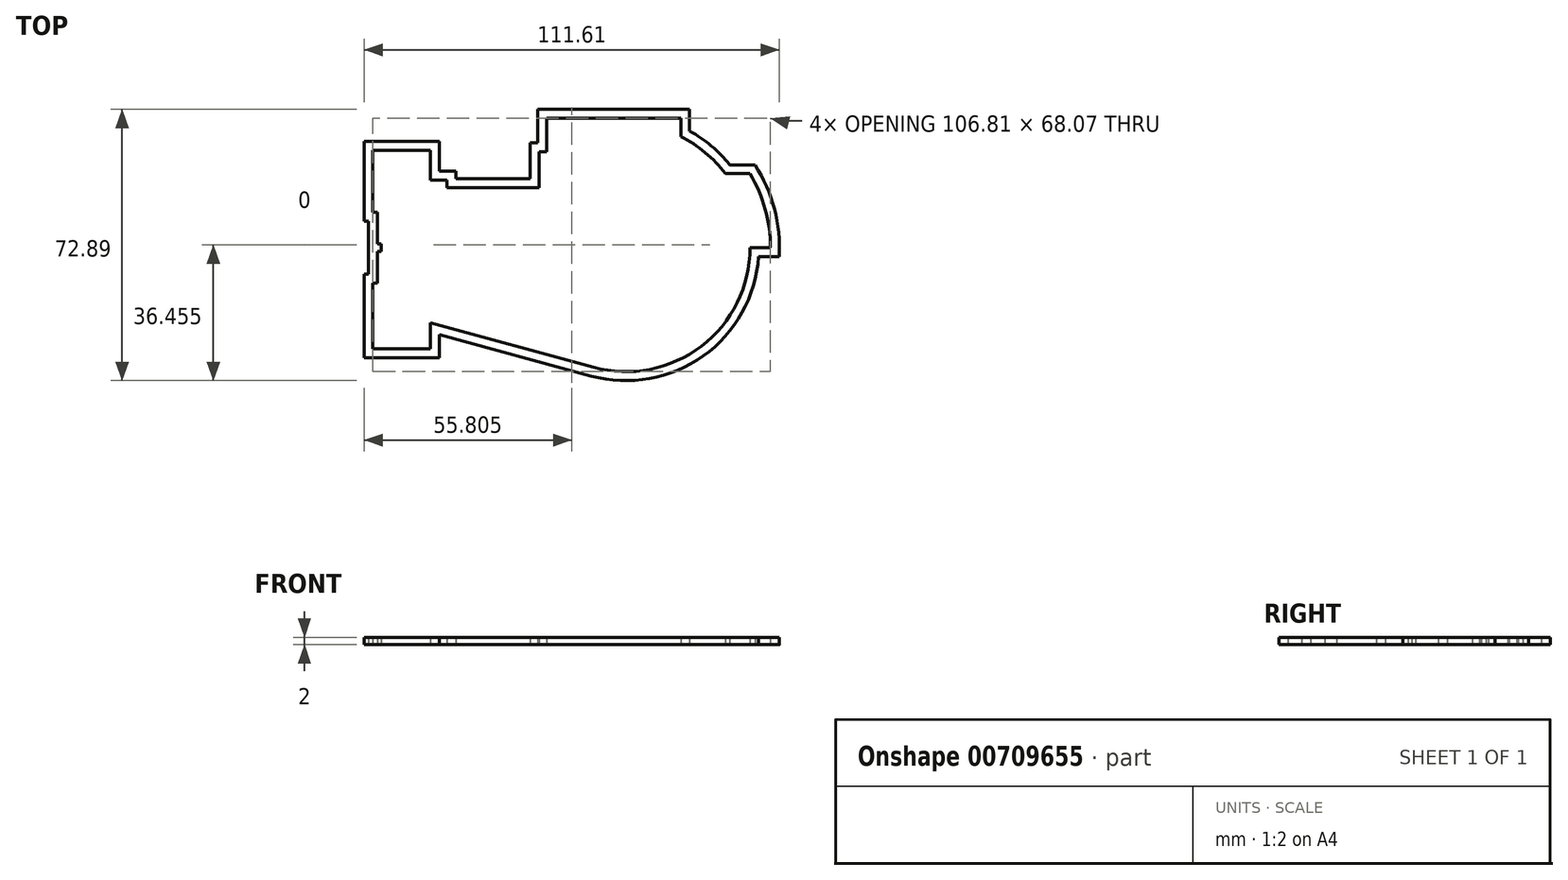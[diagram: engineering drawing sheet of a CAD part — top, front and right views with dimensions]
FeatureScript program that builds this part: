
annotation { "Feature Type Name" : "Feature", "Feature Type Description" : "" }
export const myFeature = defineFeature(function(context is Context, id is Id, definition is map)
    precondition{}
    {
        {
            var Q0;
            Q0=qCreatedBy(makeId("Top.planeOp"),FACE);
            var sketch = newSketch(context, id + "F0", { "sketchPlane" : qUnion([Q0])});
            skArc(sketch, "E0", {"start": v(-8.74, -32.13) * mm, "mid": v(20.22, -26.46) * mm, "end": v(33.3, 0) * mm});
            skArc(sketch, "E1", {"start": v(38.8, 0) * mm, "mid": v(37.4, 10.33) * mm, "end": v(33.3, 19.91) * mm});
            skLineSegment(sketch, "E2", {"start": v(33.3, 0) * mm, "end": v(38.8, 0) * mm});
            skLineSegment(sketch, "E3", {"start": v(33.3, 19.91) * mm, "end": v(26.69, 19.91) * mm});
            skLineSegment(sketch, "E4", {"start": v(-21.31, 25.79) * mm, "end": v(-23.31, 25.79) * mm});
            skArc(sketch, "E5.trimOffspring", {"start": v(26.69, 19.91) * mm, "mid": v(21.28, 25.61) * mm, "end": v(14.69, 29.88) * mm});
            skLineSegment(sketch, "E6.MirrorCS", {"start": v(-68.01, -9.5) * mm, "end": v(-66.81, -9.5) * mm});
            skLineSegment(sketch, "E7.MirrorCS", {"start": v(-65.81, -1) * mm, "end": v(-65.81, 0) * mm});
            skLineSegment(sketch, "E8.MirrorCS", {"start": v(-66.81, -1) * mm, "end": v(-65.81, -1) * mm});
            skLineSegment(sketch, "E9.MirrorCS", {"start": v(-66.81, -9.5) * mm, "end": v(-66.81, -1) * mm});
            skLineSegment(sketch, "E10", {"start": v(-52.61, 26.2) * mm, "end": v(-52.61, 18.2) * mm});
            skLineSegment(sketch, "E11", {"start": v(-23.31, 25.79) * mm, "end": v(-23.31, 16.2) * mm});
            skArc(sketch, "E12", {"start": v(204.58, -8.62) * mm, "mid": v(241.3, -32.1) * mm, "end": v(269.8, 0.86) * mm});
            skArc(sketch, "E13", {"start": v(275.3, 0.86) * mm, "mid": v(273.9, 11.2) * mm, "end": v(269.8, 20.77) * mm});
            skLineSegment(sketch, "E14", {"start": v(269.8, 0.86) * mm, "end": v(275.3, 0.86) * mm});
            skLineSegment(sketch, "E15", {"start": v(269.8, 20.77) * mm, "end": v(263.2, 20.77) * mm});
            skLineSegment(sketch, "E16", {"start": v(263.2, 20.77) * mm, "end": v(248.4, 20.77) * mm, "construction": true});
            skLineSegment(sketch, "E17", {"start": v(248.4, 20.77) * mm, "end": v(248.4, 31.97) * mm, "construction": true});
            skLineSegment(sketch, "E18", {"start": v(248.4, 31.97) * mm, "end": v(248.4, 35.97) * mm});
            skLineSegment(sketch, "E19", {"start": v(248.4, 35.97) * mm, "end": v(218.9, 35.97) * mm});
            skLineSegment(sketch, "E20", {"start": v(218.9, 35.97) * mm, "end": v(218.9, 31.97) * mm});
            skLineSegment(sketch, "E21", {"start": v(218.9, 31.97) * mm, "end": v(214.9, 31.97) * mm});
            skLineSegment(sketch, "E22", {"start": v(214.9, 31.97) * mm, "end": v(214.9, 26.97) * mm});
            skLineSegment(sketch, "E23", {"start": v(214.9, 26.97) * mm, "end": v(212.9, 26.97) * mm});
            skLineSegment(sketch, "E24", {"start": v(183.9, 26.06) * mm, "end": v(169.9, 26.06) * mm});
            skLineSegment(sketch, "E25", {"start": v(169.9, 26.06) * mm, "end": v(169.9, 10.36) * mm});
            skLineSegment(sketch, "E26", {"start": v(169.9, 10.36) * mm, "end": v(171.1, 10.36) * mm});
            skLineSegment(sketch, "E27", {"start": v(171.1, 10.36) * mm, "end": v(171.1, 1.86) * mm});
            skLineSegment(sketch, "E28", {"start": v(171.1, 1.86) * mm, "end": v(172.1, 1.86) * mm});
            skArc(sketch, "E29.trimOffspring", {"start": v(263.2, 20.77) * mm, "mid": v(256.6, 27.42) * mm, "end": v(248.4, 31.97) * mm});
            skLineSegment(sketch, "E30", {"start": v(172.1, 1.86) * mm, "end": v(172.1, 0.86) * mm});
            skLineSegment(sketch, "E31.MirrorCS", {"start": v(169.9, -8.64) * mm, "end": v(171.1, -8.64) * mm});
            skLineSegment(sketch, "E32.MirrorCS", {"start": v(172.1, -0.14) * mm, "end": v(172.1, 0.86) * mm});
            skLineSegment(sketch, "E33.MirrorCS", {"start": v(171.1, -0.14) * mm, "end": v(172.1, -0.14) * mm});
            skLineSegment(sketch, "E34.MirrorCS", {"start": v(183.9, -24.34) * mm, "end": v(169.9, -24.34) * mm});
            skLineSegment(sketch, "E35.MirrorCS", {"start": v(171.1, -8.64) * mm, "end": v(171.1, -0.14) * mm});
            skLineSegment(sketch, "E36.MirrorCS", {"start": v(169.9, -24.34) * mm, "end": v(169.9, -8.64) * mm});
            skLineSegment(sketch, "E37", {"start": v(183.9, -24.34) * mm, "end": v(183.9, -17.54) * mm});
            skLineSegment(sketch, "E38", {"start": v(183.9, 26.06) * mm, "end": v(183.9, 18.06) * mm});
            skLineSegment(sketch, "E39", {"start": v(183.9, 18.06) * mm, "end": v(186.9, 18.06) * mm});
            skLineSegment(sketch, "E40", {"start": v(186.9, 18.06) * mm, "end": v(186.9, 16.06) * mm});
            skLineSegment(sketch, "E41", {"start": v(186.9, 16.06) * mm, "end": v(213.9, 16.06) * mm});
            skLineSegment(sketch, "E42", {"start": v(212.9, 26.97) * mm, "end": v(212.9, 16.06) * mm});
            skLineSegment(sketch, "E43", {"start": v(183.9, -17.54) * mm, "end": v(226.54, -30.91) * mm});
            skLineSegment(sketch, "E44", {"start": v(-65.81, 0) * mm, "end": v(-65.81, 1) * mm});
            skLineSegment(sketch, "E45", {"start": v(-65.81, 1) * mm, "end": v(-66.81, 1) * mm});
            skLineSegment(sketch, "E46", {"start": v(-66.81, 1) * mm, "end": v(-66.81, 9.5) * mm});
            skLineSegment(sketch, "E47", {"start": v(-66.81, 9.5) * mm, "end": v(-68.01, 9.5) * mm});
            skLineSegment(sketch, "E48", {"start": v(-68.01, 9.5) * mm, "end": v(-68.01, 26.2) * mm});
            skLineSegment(sketch, "E49", {"start": v(-48.11, 16.2) * mm, "end": v(-23.31, 16.2) * mm});
            skLineSegment(sketch, "E50", {"start": v(-68.01, -9.5) * mm, "end": v(-68.01, -27.2) * mm});
            skArc(sketch, "E51", {"start": v(230.7, -116.63) * mm, "mid": v(260.39, -111.7) * mm, "end": v(273.97, -84.85) * mm});
            skArc(sketch, "E52", {"start": v(279.47, -84.85) * mm, "mid": v(278.07, -74.53) * mm, "end": v(273.97, -64.94) * mm});
            skLineSegment(sketch, "E53", {"start": v(273.97, -84.85) * mm, "end": v(279.47, -84.85) * mm});
            skLineSegment(sketch, "E54", {"start": v(273.97, -64.94) * mm, "end": v(267.36, -64.94) * mm});
            skLineSegment(sketch, "E55", {"start": v(253.36, -54.07) * mm, "end": v(253.36, -50.07) * mm});
            skLineSegment(sketch, "E56", {"start": v(253.36, -50.07) * mm, "end": v(223.36, -50.07) * mm});
            skLineSegment(sketch, "E57", {"start": v(223.36, -50.07) * mm, "end": v(223.36, -54.07) * mm});
            skLineSegment(sketch, "E58", {"start": v(223.36, -54.07) * mm, "end": v(219.36, -54.07) * mm});
            skLineSegment(sketch, "E59", {"start": v(219.36, -54.07) * mm, "end": v(219.36, -59.07) * mm});
            skLineSegment(sketch, "E60", {"start": v(219.36, -59.07) * mm, "end": v(217.36, -59.07) * mm});
            skLineSegment(sketch, "E61", {"start": v(188.06, -58.65) * mm, "end": v(174.06, -58.65) * mm});
            skArc(sketch, "E62.trimOffspring", {"start": v(267.36, -64.94) * mm, "mid": v(261.1, -58.56) * mm, "end": v(253.36, -54.07) * mm});
            skLineSegment(sketch, "E63.MirrorCS", {"start": v(174.06, -94.35) * mm, "end": v(175.26, -94.35) * mm});
            skLineSegment(sketch, "E64.MirrorCS", {"start": v(176.26, -85.85) * mm, "end": v(176.26, -84.85) * mm});
            skLineSegment(sketch, "E65.MirrorCS", {"start": v(175.26, -85.85) * mm, "end": v(176.26, -85.85) * mm});
            skLineSegment(sketch, "E66.MirrorCS", {"start": v(175.26, -94.35) * mm, "end": v(175.26, -85.85) * mm});
            skLineSegment(sketch, "E67", {"start": v(188.06, -58.65) * mm, "end": v(188.06, -66.65) * mm});
            skLineSegment(sketch, "E68", {"start": v(188.06, -66.65) * mm, "end": v(191.06, -66.65) * mm});
            skLineSegment(sketch, "E69", {"start": v(191.06, -66.65) * mm, "end": v(191.06, -68.65) * mm});
            skLineSegment(sketch, "E70", {"start": v(217.36, -59.07) * mm, "end": v(217.36, -68.65) * mm});
            skLineSegment(sketch, "E71", {"start": v(240.67, -84.85) * mm, "end": v(176.26, -84.85) * mm});
            skLineSegment(sketch, "E72", {"start": v(176.26, -84.85) * mm, "end": v(176.26, -83.85) * mm});
            skLineSegment(sketch, "E73", {"start": v(176.26, -83.85) * mm, "end": v(175.26, -83.85) * mm});
            skLineSegment(sketch, "E74", {"start": v(175.26, -83.85) * mm, "end": v(175.26, -75.35) * mm});
            skLineSegment(sketch, "E75", {"start": v(175.26, -75.35) * mm, "end": v(174.06, -75.35) * mm});
            skLineSegment(sketch, "E76", {"start": v(174.06, -75.35) * mm, "end": v(174.06, -58.65) * mm});
            skLineSegment(sketch, "E77", {"start": v(191.06, -68.65) * mm, "end": v(217.36, -68.65) * mm});
            skLineSegment(sketch, "E78", {"start": v(174.06, -94.35) * mm, "end": v(174.06, -112.05) * mm});
            skLineSegment(sketch, "E79", {"start": v(174.06, -112.05) * mm, "end": v(188.06, -112.05) * mm});
            skLineSegment(sketch, "E80", {"start": v(188.06, -112.05) * mm, "end": v(188.06, -103.25) * mm});
            skLineSegment(sketch, "E81", {"start": v(188.06, -103.25) * mm, "end": v(230.7, -116.63) * mm});
            skLineSegment(sketch, "E82", {"start": v(-68.01, 26.2) * mm, "end": v(-52.61, 26.2) * mm});
            skLineSegment(sketch, "E83", {"start": v(-68.01, -27.2) * mm, "end": v(-52.61, -27.2) * mm});
            skLineSegment(sketch, "E84", {"start": v(14.69, 34.79) * mm, "end": v(14.69, 29.88) * mm});
            skPoint(sketch, "E85.orphan", {"position": v(12.69, 30.79) * mm});
            skLineSegment(sketch, "E86", {"start": v(-48.11, 18.2) * mm, "end": v(-48.11, 16.2) * mm});
            skPoint(sketch, "E87.orphan", {"position": v(-49.61, 16.2) * mm});
            skLineSegment(sketch, "E88", {"start": v(-52.61, 18.2) * mm, "end": v(-48.11, 18.2) * mm});
            skLineSegment(sketch, "E89", {"start": v(-52.61, -27.2) * mm, "end": v(-52.61, -20.2) * mm});
            skLineSegment(sketch, "E90", {"start": v(-52.61, -20.2) * mm, "end": v(-8.74, -32.13) * mm});
            skLineSegment(sketch, "E91", {"start": v(-21.31, 34.79) * mm, "end": v(14.69, 34.79) * mm});
            skLineSegment(sketch, "E92", {"start": v(-21.31, 34.79) * mm, "end": v(-21.31, 25.79) * mm});
            skLineSegment(sketch, "E93.0", {"start": v(-70.41, -29.6) * mm, "end": v(-50.21, -29.6) * mm});
            skLineSegment(sketch, "E93.1", {"start": v(-23.71, 28.19) * mm, "end": v(-25.71, 28.19) * mm});
            skLineSegment(sketch, "E93.2", {"start": v(-23.71, 37.19) * mm, "end": v(-23.71, 28.19) * mm});
            skLineSegment(sketch, "E93.3", {"start": v(-23.71, 37.19) * mm, "end": v(17.09, 37.19) * mm});
            skLineSegment(sketch, "E93.4", {"start": v(17.09, 37.19) * mm, "end": v(17.09, 31.34) * mm});
            skArc(sketch, "E93.5", {"start": v(27.87, 22.31) * mm, "mid": v(22.93, 27.36) * mm, "end": v(17.09, 31.34) * mm});
            skLineSegment(sketch, "E93.6", {"start": v(34.63, 22.31) * mm, "end": v(27.87, 22.31) * mm});
            skLineSegment(sketch, "E93.7", {"start": v(-50.21, -23.34) * mm, "end": v(-9.37, -34.45) * mm});
            skArc(sketch, "E93.8", {"start": v(-9.37, -34.45) * mm, "mid": v(20.71, -29.08) * mm, "end": v(35.62, -2.4) * mm});
            skLineSegment(sketch, "E93.9", {"start": v(35.62, -2.4) * mm, "end": v(41.13, -2.4) * mm});
            skArc(sketch, "E93.10", {"start": v(41.13, -2.4) * mm, "mid": v(39.85, 10.47) * mm, "end": v(34.63, 22.31) * mm});
            skLineSegment(sketch, "E93.11", {"start": v(-25.71, 28.19) * mm, "end": v(-25.71, 18.6) * mm});
            skLineSegment(sketch, "E93.12", {"start": v(-50.21, -29.6) * mm, "end": v(-50.21, -23.34) * mm});
            skLineSegment(sketch, "E93.13", {"start": v(-45.71, 18.6) * mm, "end": v(-25.71, 18.6) * mm});
            skLineSegment(sketch, "E93.14", {"start": v(-45.71, 20.6) * mm, "end": v(-45.71, 18.6) * mm});
            skLineSegment(sketch, "E93.15", {"start": v(-50.21, 20.6) * mm, "end": v(-45.71, 20.6) * mm});
            skLineSegment(sketch, "E93.16", {"start": v(-50.21, 28.6) * mm, "end": v(-50.21, 20.6) * mm});
            skLineSegment(sketch, "E93.17", {"start": v(-70.41, 28.6) * mm, "end": v(-50.21, 28.6) * mm});
            skLineSegment(sketch, "E93.18", {"start": v(-70.41, 7.1) * mm, "end": v(-70.41, 28.6) * mm});
            skLineSegment(sketch, "E93.19", {"start": v(-69.21, 7.1) * mm, "end": v(-70.41, 7.1) * mm});
            skLineSegment(sketch, "E93.20", {"start": v(-69.21, 1.4) * mm, "end": v(-69.21, 7.1) * mm});
            skLineSegment(sketch, "E93.21", {"start": v(-69.21, -7.1) * mm, "end": v(-69.21, 1.4) * mm});
            skLineSegment(sketch, "E93.22", {"start": v(-70.41, -7.1) * mm, "end": v(-69.21, -7.1) * mm});
            skLineSegment(sketch, "E93.23", {"start": v(-70.41, -7.1) * mm, "end": v(-70.41, -29.6) * mm});
            skSolve(sketch);
        }
        {
            var Q0;
            Q0=makeQuery(id+"F0.imprint","IMPRINT",FACE,{"disambiguationData":[TD([[makeQuery(id+"F0.imprint","IMPRINT",EDGE,{"derivedFrom":sQuery(id+"F0.wireOp",EDGE,"E0")}),-1.0]])]});
            extrude(context, id + "F1", {"entities" : qUnion([Q0]), "depth" : 2 * mm, "offsetDistance" : 25 * mm, "symmetric" : true});
        }
    });
